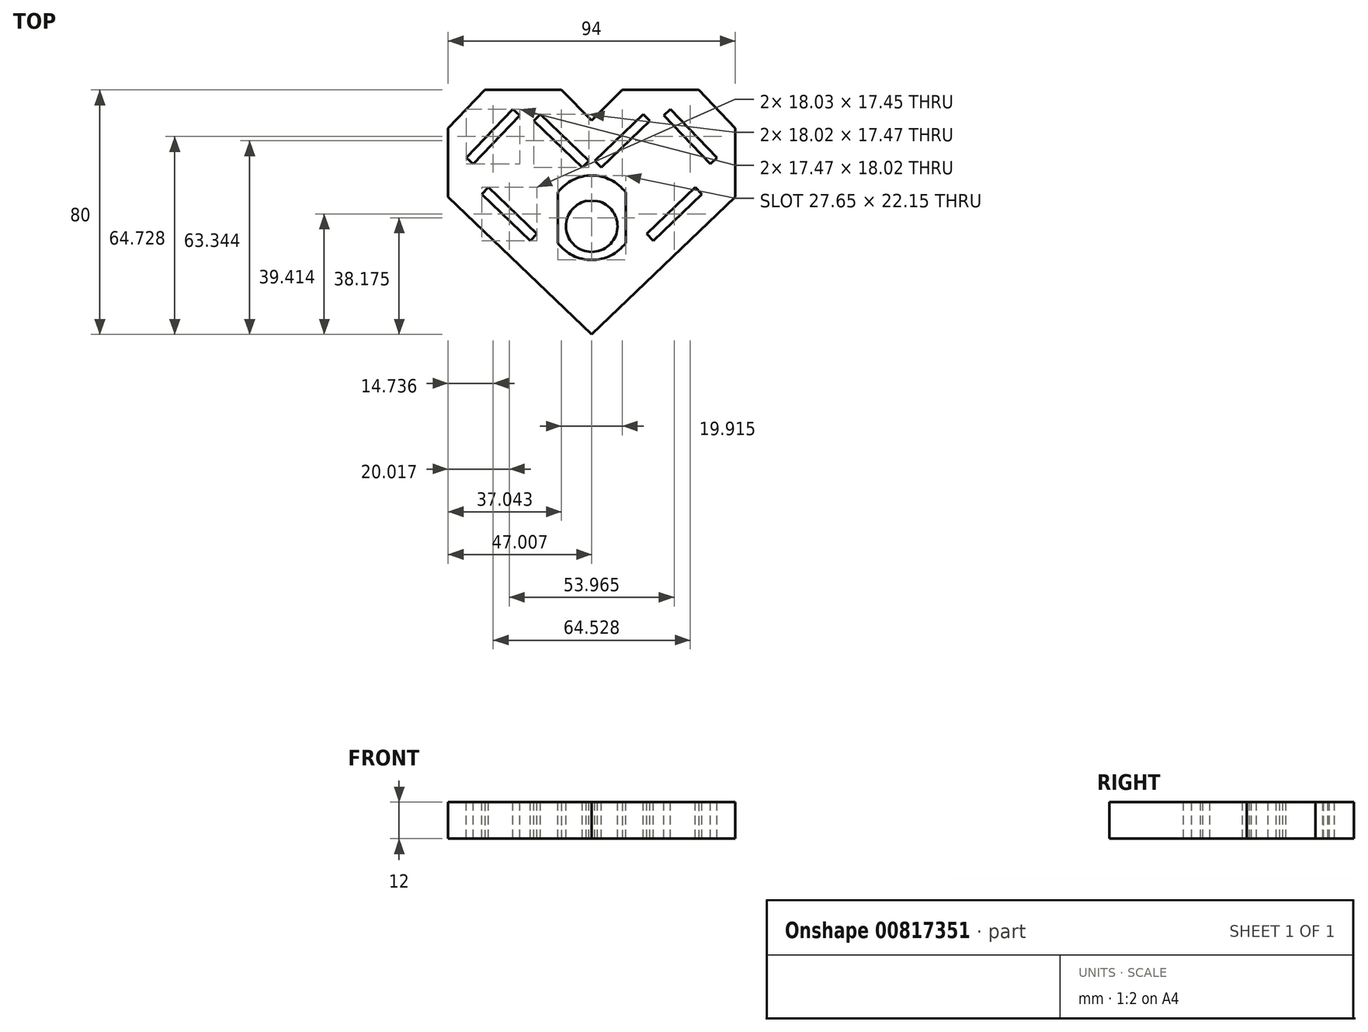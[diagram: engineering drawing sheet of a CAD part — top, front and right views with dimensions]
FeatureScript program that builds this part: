
annotation { "Feature Type Name" : "Feature", "Feature Type Description" : "" }
export const myFeature = defineFeature(function(context is Context, id is Id, definition is map)
    precondition{}
    {
        {
            var Q0;
            Q0=qCreatedBy(makeId("Top.planeOp"),FACE);
            var sketch = newSketch(context, id + "F0", { "sketchPlane" : qUnion([Q0])});
            skLineSegment(sketch, "E0", {"start": v(0, -61) * mm, "end": v(47, -16) * mm});
            skLineSegment(sketch, "E1", {"start": v(47, -16) * mm, "end": v(47, 6.5) * mm});
            skLineSegment(sketch, "E2", {"start": v(47, 6.5) * mm, "end": v(35, 19) * mm});
            skLineSegment(sketch, "E3", {"start": v(35, 19) * mm, "end": v(10, 19) * mm});
            skLineSegment(sketch, "E4", {"start": v(10, 19) * mm, "end": v(0, 9) * mm});
            skLineSegment(sketch, "E5.MirrorCS", {"start": v(-10, 19) * mm, "end": v(0, 9) * mm});
            skLineSegment(sketch, "E6.MirrorCS", {"start": v(-35, 19) * mm, "end": v(-10, 19) * mm});
            skLineSegment(sketch, "E7.MirrorCS", {"start": v(-47, 6.5) * mm, "end": v(-35, 19) * mm});
            skLineSegment(sketch, "E8.MirrorCS", {"start": v(-47, -16) * mm, "end": v(-47, 6.5) * mm});
            skLineSegment(sketch, "E9.MirrorCS", {"start": v(0, -61) * mm, "end": v(-47, -16) * mm});
            skSolve(sketch);
        }
        {
            var Q0;
            Q0=qSketchRegion(id+"F0",true);
            extrude(context, id + "F1", {"entities" : qUnion([Q0]), "depth" : 12 * mm, "offsetDistance" : 25 * mm});
        }
        {
            var Q0;
            Q0=makeQuery(id+"F1.opExtrude","CAP_FACE",FACE,{"disambiguationData":[OSD([sQuery(id+"F0.wireOp",EDGE,"E0"),sQuery(id+"F0.wireOp",EDGE,"E1"),sQuery(id+"F0.wireOp",EDGE,"E2"),sQuery(id+"F0.wireOp",EDGE,"E3"),sQuery(id+"F0.wireOp",EDGE,"E4"),sQuery(id+"F0.wireOp",EDGE,"82c20e4c-a16d-44ab-ba3a-01f44a2a79d4.MirrorCS"),sQuery(id+"F0.wireOp",EDGE,"ec838d24-a44d-4492-aded-78a89141ed91.MirrorCS"),sQuery(id+"F0.wireOp",EDGE,"bd7d52e1-2083-4ff2-afdd-3f343d5251aa.MirrorCS"),sQuery(id+"F0.wireOp",EDGE,"4fc21238-a6f4-42ad-b0c3-35517250600e.MirrorCS"),sQuery(id+"F0.wireOp",EDGE,"0c5398ae-afa2-41ec-94e7-8fb47a1d7522.MirrorCS")])],"isStart":false});
            var sketch = newSketch(context, id + "F2", { "sketchPlane" : qUnion([Q0])});
            skLineSegment(sketch, "E10", {"start": v(41, -3.13) * mm, "end": v(25.76, 12.74) * mm});
            skLineSegment(sketch, "E11", {"start": v(41, -3.13) * mm, "end": v(38.76, -5.28) * mm});
            skLineSegment(sketch, "E12", {"start": v(38.76, -5.28) * mm, "end": v(23.53, 10.59) * mm});
            skLineSegment(sketch, "E13", {"start": v(23.53, 10.59) * mm, "end": v(25.76, 12.74) * mm});
            skLineSegment(sketch, "E14.MirrorCS", {"start": v(-23.53, 10.59) * mm, "end": v(-25.76, 12.74) * mm});
            skLineSegment(sketch, "E15.MirrorCS", {"start": v(-41, -3.13) * mm, "end": v(-25.76, 12.74) * mm});
            skLineSegment(sketch, "E16.MirrorCS", {"start": v(-38.76, -5.28) * mm, "end": v(-23.53, 10.59) * mm});
            skLineSegment(sketch, "E17.MirrorCS", {"start": v(-41, -3.13) * mm, "end": v(-38.76, -5.28) * mm});
            skLineSegment(sketch, "E18", {"start": v(18.97, 8.84) * mm, "end": v(3.1, -6.4) * mm});
            skLineSegment(sketch, "E19", {"start": v(3.1, -6.4) * mm, "end": v(0.95, -4.16) * mm});
            skLineSegment(sketch, "E20", {"start": v(0.95, -4.16) * mm, "end": v(16.82, 11.08) * mm});
            skLineSegment(sketch, "E21", {"start": v(16.82, 11.08) * mm, "end": v(18.97, 8.84) * mm});
            skLineSegment(sketch, "E22", {"start": v(-11, -42.16) * mm, "end": v(11, -42.16) * mm});
            skLineSegment(sketch, "E23", {"start": v(11, -42.16) * mm, "end": v(-11, -42.16) * mm});
            skLineSegment(sketch, "E24", {"start": v(-11, -39.06) * mm, "end": v(-11, -42.16) * mm});
            skLineSegment(sketch, "E25", {"start": v(-11, -39.06) * mm, "end": v(11, -39.06) * mm});
            skLineSegment(sketch, "E26", {"start": v(11, -39.06) * mm, "end": v(11, -42.16) * mm});
            skPoint(sketch, "E27.start.orphan", {"position": v(17.97, -28.07) * mm});
            skPoint(sketch, "E28.start.orphan", {"position": v(20.1, -30.31) * mm});
            skPoint(sketch, "E29.end.orphan", {"position": v(36, -15.1) * mm});
            skPoint(sketch, "E29.start.orphan", {"position": v(33.86, -12.86) * mm});
            skLineSegment(sketch, "E30", {"start": v(20.1, -30.31) * mm, "end": v(36, -15.1) * mm});
            skLineSegment(sketch, "E31", {"start": v(33.86, -12.86) * mm, "end": v(36, -15.1) * mm});
            skLineSegment(sketch, "E32", {"start": v(33.86, -12.86) * mm, "end": v(17.97, -28.07) * mm});
            skLineSegment(sketch, "E33", {"start": v(17.97, -28.07) * mm, "end": v(20.1, -30.31) * mm});
            skPoint(sketch, "E34.MirrorCS.end.orphan", {"position": v(-17.97, -28.07) * mm});
            skPoint(sketch, "E34.MirrorCS.start.orphan", {"position": v(-20.1, -30.31) * mm});
            skPoint(sketch, "E35.MirrorCS.end.orphan", {"position": v(-33.86, -12.86) * mm});
            skPoint(sketch, "E36.MirrorCS.end.orphan", {"position": v(-36, -15.1) * mm});
            skLineSegment(sketch, "E37.MirrorCS", {"start": v(-33.86, -12.86) * mm, "end": v(-17.97, -28.07) * mm});
            skLineSegment(sketch, "E38.MirrorCS", {"start": v(-20.1, -30.31) * mm, "end": v(-36, -15.1) * mm});
            skLineSegment(sketch, "E39.MirrorCS", {"start": v(-17.97, -28.07) * mm, "end": v(-20.1, -30.31) * mm});
            skLineSegment(sketch, "E40.MirrorCS", {"start": v(-33.86, -12.86) * mm, "end": v(-36, -15.1) * mm});
            skLineSegment(sketch, "E41.MirrorCS", {"start": v(-3.1, -6.4) * mm, "end": v(-0.95, -4.16) * mm});
            skLineSegment(sketch, "E42.MirrorCS", {"start": v(-0.95, -4.16) * mm, "end": v(-16.82, 11.08) * mm});
            skLineSegment(sketch, "E43.MirrorCS", {"start": v(-18.97, 8.84) * mm, "end": v(-3.1, -6.4) * mm});
            skLineSegment(sketch, "E44.MirrorCS", {"start": v(-16.82, 11.08) * mm, "end": v(-18.97, 8.84) * mm});
            skArc(sketch, "E45", {"start": v(-11.07, -31.1) * mm, "mid": v(0, -36.65) * mm, "end": v(11.08, -31.1) * mm});
            skLineSegment(sketch, "E46.right", {"start": v(-11.07, -14.55) * mm, "end": v(-11.07, -31.1) * mm});
            skLineSegment(sketch, "E47.right", {"start": v(11.08, -14.55) * mm, "end": v(11.08, -31.1) * mm});
            skArc(sketch, "E48.trimOffspring", {"start": v(11.08, -14.55) * mm, "mid": v(0, -9) * mm, "end": v(-11.07, -14.55) * mm});
            skArc(sketch, "E49", {"start": v(-1.84, -17.35) * mm, "mid": v(-0.03, -34) * mm, "end": v(1.86, -17.36) * mm});
            skLineSegment(sketch, "E50", {"start": v(-1.84, -17.35) * mm, "end": v(1.86, -17.36) * mm});
            skLineSegment(sketch, "E51", {"start": v(-47, 6.5) * mm, "end": v(-35, 19) * mm});
            skLineSegment(sketch, "E52", {"start": v(-35, 19) * mm, "end": v(-10, 19) * mm});
            skLineSegment(sketch, "E53", {"start": v(-10, 19) * mm, "end": v(0, 9) * mm});
            skLineSegment(sketch, "E54", {"start": v(0, 9) * mm, "end": v(10, 19) * mm});
            skLineSegment(sketch, "E55", {"start": v(10, 19) * mm, "end": v(35, 19) * mm});
            skLineSegment(sketch, "E56", {"start": v(35, 19) * mm, "end": v(47, 6.5) * mm});
            skLineSegment(sketch, "E57", {"start": v(47, 6.5) * mm, "end": v(47, -16) * mm});
            skLineSegment(sketch, "E58", {"start": v(47, -16) * mm, "end": v(0, -61) * mm});
            skLineSegment(sketch, "E59", {"start": v(0, -61) * mm, "end": v(-47, -16) * mm});
            skLineSegment(sketch, "E60", {"start": v(-47, -16) * mm, "end": v(-47, 6.5) * mm});
            skSolve(sketch);
        }
        {
            var Q0;
            Q0=makeQuery(id+"F2.imprint","IMPRINT",FACE,{"disambiguationData":[TD([[makeQuery(id+"F2.imprint","IMPRINT",EDGE,{"derivedFrom":sQuery(id+"F2.wireOp",EDGE,"E10")}),1.0]])]});
            var Q1;
            Q1=makeQuery(id+"F2.imprint","IMPRINT",FACE,{"disambiguationData":[TD([[makeQuery(id+"F2.imprint","IMPRINT",EDGE,{"derivedFrom":sQuery(id+"F2.wireOp",EDGE,"E30")}),1.0]])]});
            var Q2;
            Q2=makeQuery(id+"F2.imprint","IMPRINT",FACE,{"disambiguationData":[TD([[makeQuery(id+"F2.imprint","IMPRINT",EDGE,{"derivedFrom":sQuery(id+"F2.wireOp",EDGE,"E23")}),-1.0]])]});
            var Q3;
            Q3=makeQuery(id+"F2.imprint","IMPRINT",FACE,{"disambiguationData":[TD([[makeQuery(id+"F2.imprint","IMPRINT",EDGE,{"derivedFrom":sQuery(id+"F2.wireOp",EDGE,"E37.MirrorCS")}),-1.0]])]});
            var Q4;
            Q4=makeQuery(id+"F2.imprint","IMPRINT",FACE,{"disambiguationData":[TD([[makeQuery(id+"F2.imprint","IMPRINT",EDGE,{"derivedFrom":sQuery(id+"F2.wireOp",EDGE,"E18")}),-1.0]])]});
            var Q5;
            Q5=makeQuery(id+"F2.imprint","IMPRINT",FACE,{"disambiguationData":[TD([[makeQuery(id+"F2.imprint","IMPRINT",EDGE,{"derivedFrom":sQuery(id+"F2.wireOp",EDGE,"E41.MirrorCS")}),1.0]])]});
            var Q6;
            Q6=makeQuery(id+"F2.imprint","IMPRINT",FACE,{"disambiguationData":[TD([[makeQuery(id+"F2.imprint","IMPRINT",EDGE,{"derivedFrom":sQuery(id+"F2.wireOp",EDGE,"E14.MirrorCS")}),1.0]])]});
            var Q7;
            Q7=makeQuery(id+"F2.imprint","IMPRINT",FACE,{"disambiguationData":[TD([[makeQuery(id+"F2.imprint","IMPRINT",EDGE,{"derivedFrom":sQuery(id+"F2.wireOp",EDGE,"ab1e3101-fcbb-46e0-a856-f4acf97266c3")}),1.0]])]});
            var Q8;
            Q8=makeQuery(id+"F2.imprint","IMPRINT",FACE,{"disambiguationData":[TD([[makeQuery(id+"F2.imprint","IMPRINT",EDGE,{"derivedFrom":sQuery(id+"F2.wireOp",EDGE,"E45")}),1.0]])]});
            extrude(context, id + "F3", {"entities" : qUnion([Q0, Q1, Q2, Q3, Q4, Q5, Q6, Q7, Q8]), "operationType" : NewBodyOperationType.REMOVE, "oppositeDirection" : true, "depth" : 25 * mm, "offsetDistance" : 25 * mm});
        }
    });
